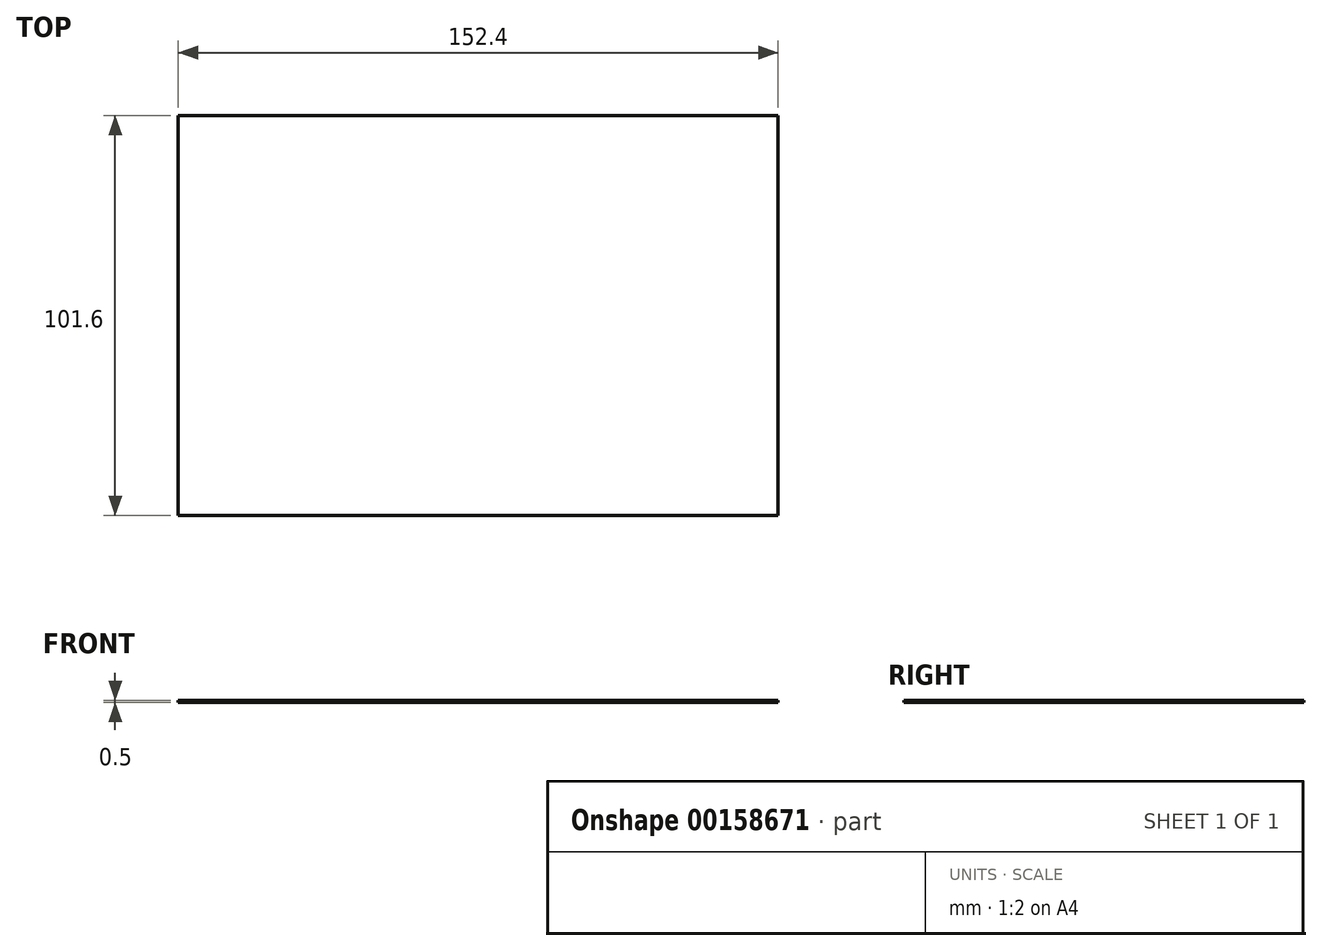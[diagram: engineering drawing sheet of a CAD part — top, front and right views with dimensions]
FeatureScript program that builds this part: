
annotation { "Feature Type Name" : "Feature", "Feature Type Description" : "" }
export const myFeature = defineFeature(function(context is Context, id is Id, definition is map)
    precondition{}
    {
        {
            var Q0;
            Q0=qCreatedBy(makeId("Top.planeOp"),FACE);
            var sketch = newSketch(context, id + "F0", { "sketchPlane" : qUnion([Q0])});
            skLineSegment(sketch, "E0.bottom", {"start": v(76.2, 50.8) * mm, "end": v(-76.2, 50.8) * mm});
            skLineSegment(sketch, "E0.top", {"start": v(76.2, -50.8) * mm, "end": v(-76.2, -50.8) * mm});
            skLineSegment(sketch, "E0.left", {"start": v(76.2, 50.8) * mm, "end": v(76.2, -50.8) * mm});
            skLineSegment(sketch, "E0.right", {"start": v(-76.2, 50.8) * mm, "end": v(-76.2, -50.8) * mm});
            skPoint(sketch, "E0.middle", {"position": v(0, 0) * mm});
            skSolve(sketch);
        }
        {
            var Q0;
            Q0=makeQuery(id+"F0.imprint","IMPRINT",FACE,{"disambiguationData":[TD([[makeQuery(id+"F0.imprint","IMPRINT",EDGE,{"derivedFrom":sQuery(id+"F0.wireOp",EDGE,"E0.bottom")}),1.0]])]});
            extrude(context, id + "F1", {"entities" : qUnion([Q0]), "depth" : .5 * mm});
        }
    });
